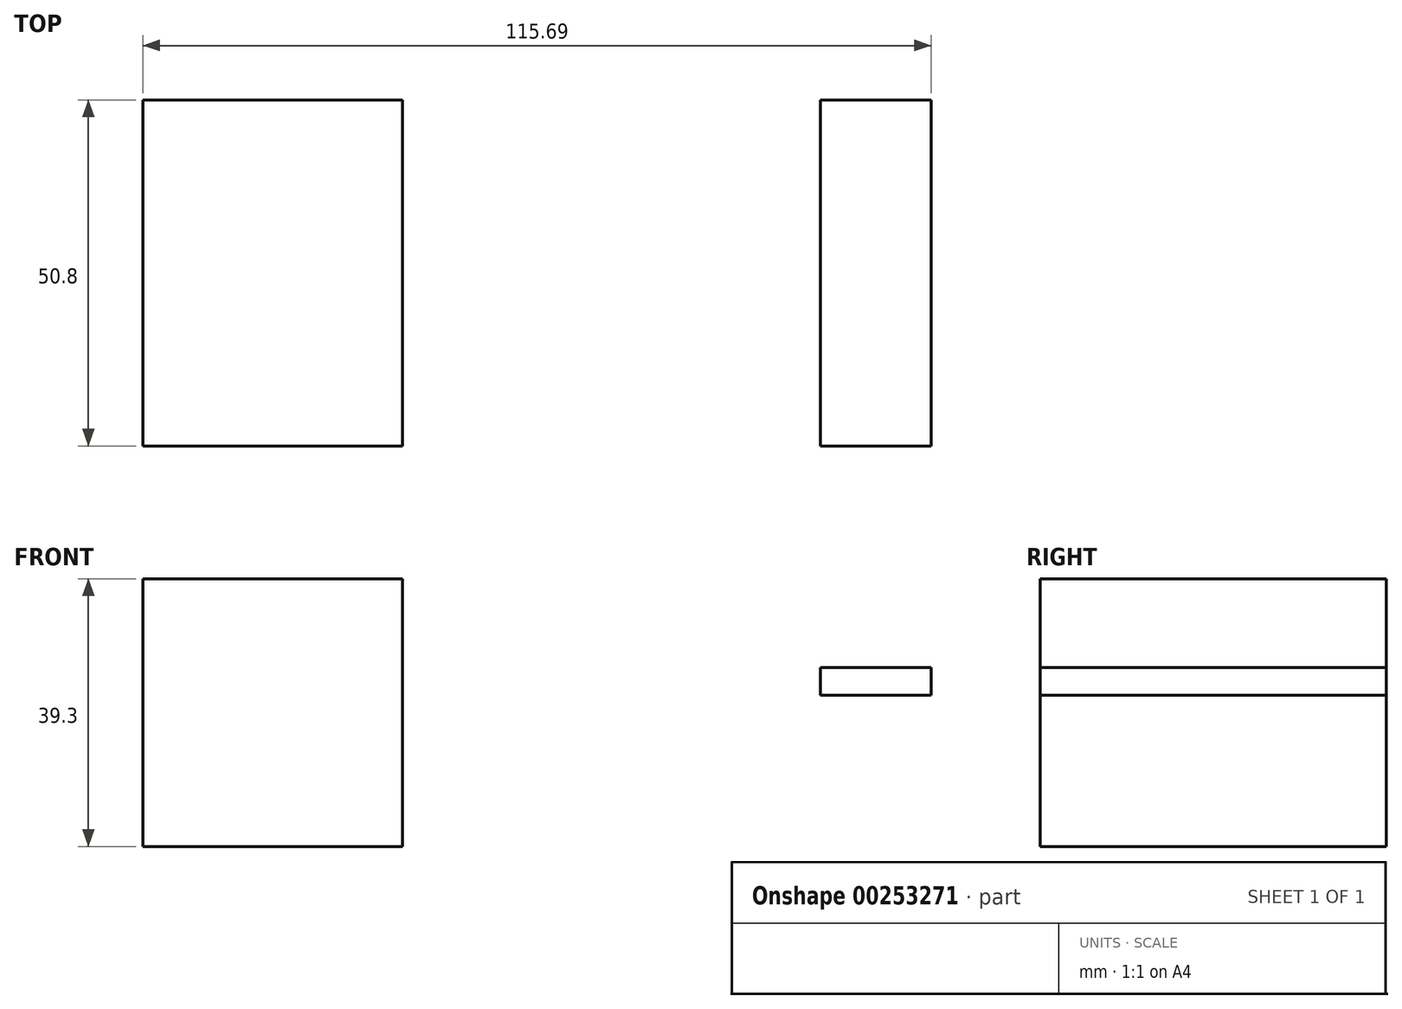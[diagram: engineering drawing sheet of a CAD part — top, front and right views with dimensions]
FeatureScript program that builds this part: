
annotation { "Feature Type Name" : "Feature", "Feature Type Description" : "" }
export const myFeature = defineFeature(function(context is Context, id is Id, definition is map)
    precondition{}
    {
        {
            var Q0;
            Q0=qCreatedBy(makeId("Front.planeOp"),FACE);
            var sketch = newSketch(context, id + "F0", { "sketchPlane" : qUnion([Q0])});
            skLineSegment(sketch, "E0.bottom", {"start": v(0, 0) * mm, "end": v(38.11, 0) * mm});
            skLineSegment(sketch, "E0.top", {"start": v(0, 39.3) * mm, "end": v(38.11, 39.3) * mm});
            skLineSegment(sketch, "E0.left", {"start": v(0, 0) * mm, "end": v(0, 39.3) * mm});
            skLineSegment(sketch, "E0.right", {"start": v(38.11, 0) * mm, "end": v(38.11, 39.3) * mm});
            skLineSegment(sketch, "E1.bottom", {"start": v(115.7, 22.19) * mm, "end": v(99.43, 22.19) * mm});
            skLineSegment(sketch, "E1.top", {"start": v(115.7, 26.26) * mm, "end": v(99.43, 26.26) * mm});
            skLineSegment(sketch, "E1.left", {"start": v(115.7, 22.19) * mm, "end": v(115.7, 26.26) * mm});
            skLineSegment(sketch, "E1.right", {"start": v(99.43, 22.19) * mm, "end": v(99.43, 26.26) * mm});
            skSolve(sketch);
        }
        {
            var Q0;
            Q0 = qSketchRegion(id + "F0", true);
            extrude(context, id + "F1", {"entities" : qUnion([Q0]), "depth" : 50.8 * mm});
        }
    });
